# Revit family: QF_Vollrath_FC-HCF-03120
name_source: partatom
category: Specialty Equipment
units: mm (PartAtom-declared; Revit-internal decimal feet)

## family parameters
Always vertical = Yes
Cut with Voids When Loaded = Yes
OmniClass Number = 23.40.40.00
OmniClass Title = Food Service Equipment and Furnishings
Part Type = Normal
Room Calculation Point = No
Round Connector Dimension = Use Diameter
Shared = No
Work Plane-Based = Yes

## types (1)
- FC-6HC-03120 (120/60/1)
    Apparent Power = 1860 VA
    Assembly Code = E1090320
    CSI MasterFormat = 11 46 16
    Conn Conduit = Yes
    Conn Plug = NEMA 5-20P
    Cutout Depth = 25.25 "
    Cutout Width = 49 "
    Cycle = 60 Hz
    Default Elevation = 0 "
    Depth = 26 "
    Description = Drop-In, Hot/Cold
    Electric Connection Type = 0
    FL Amps = 16 A
    Foodservice Equipment Identifier = Yes
    HP = .25
    Indirect Waste Connection Height = -14.5 "
    Indirect Waste Size = 1"
    Indirect Waste Size OD = 1"
    KCL SpecSheet URL = http://kcl5.kclcad.com
    Manufacturer = Vollrath
    Model = FC-6HC-03120
    Phase = 1
    URL = www.vollrath.com
    Volts = 120 V
    Watts = 1875 W
    Weight in Pounds = 212
    Width = 49.782 "

## geometry (parser evidence)
native form markers: Sweep x2
no freeform markers — native parametric forms only
